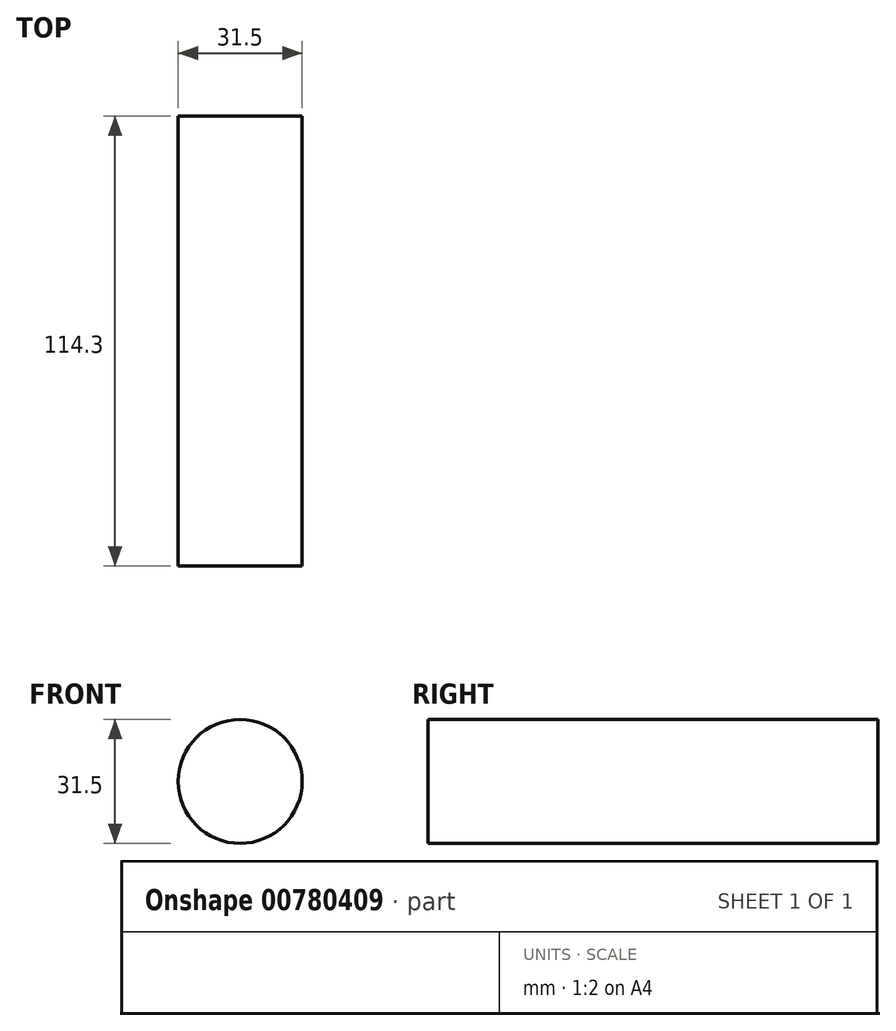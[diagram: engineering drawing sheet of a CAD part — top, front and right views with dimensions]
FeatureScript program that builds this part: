
annotation { "Feature Type Name" : "Feature", "Feature Type Description" : "" }
export const myFeature = defineFeature(function(context is Context, id is Id, definition is map)
    precondition{}
    {
        {
            var Q0;
            Q0=qCreatedBy(makeId("Front.planeOp"),FACE);
            var sketch = newSketch(context, id + "F0", { "sketchPlane" : qUnion([Q0])});
            skCircle(sketch, "E0", {"center": v(0, 0) * mm, "radius": 15.75 * mm});
            skSolve(sketch);
        }
        {
            var Q0;
            Q0=makeQuery(id+"F0.imprint","IMPRINT",FACE,{"disambiguationData":[TD([[makeQuery(id+"F0.imprint","IMPRINT",EDGE,{"derivedFrom":sQuery(id+"F0.wireOp",EDGE,"E0")}),1.0]])]});
            extrude(context, id + "F1", {"entities" : qUnion([Q0]), "depth" : 114.3 * mm, "offsetDistance" : 25.4 * mm});
        }
    });
